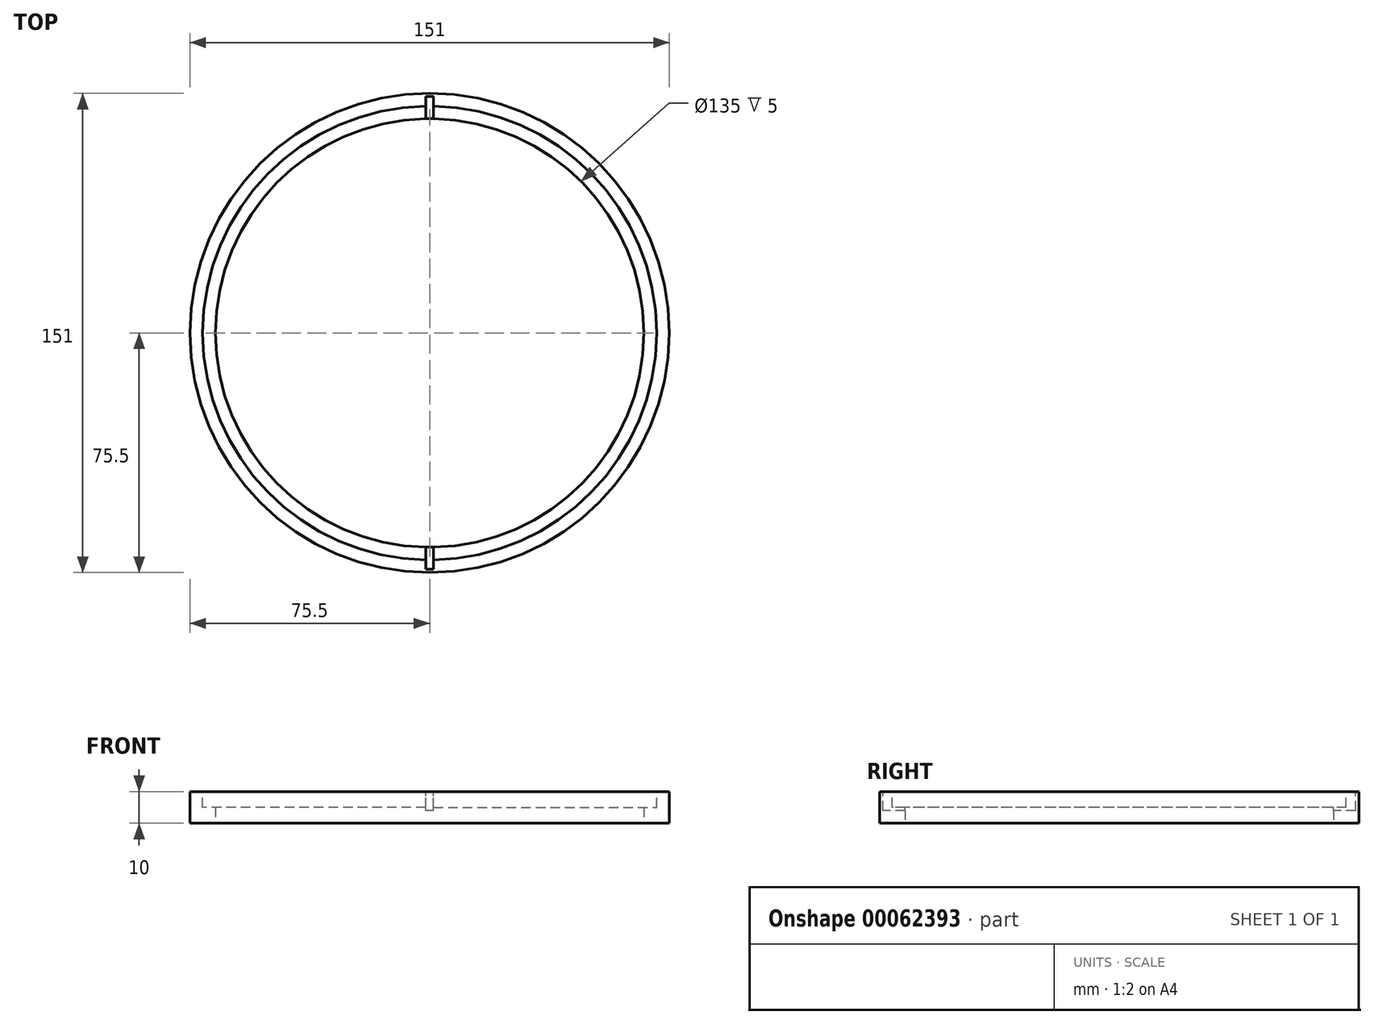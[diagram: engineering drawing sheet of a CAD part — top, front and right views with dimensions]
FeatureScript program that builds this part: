
annotation { "Feature Type Name" : "Feature", "Feature Type Description" : "" }
export const myFeature = defineFeature(function(context is Context, id is Id, definition is map)
    precondition{}
    {
        {
            var Q0;
            Q0=qCreatedBy(makeId("Top.planeOp"),FACE);
            var sketch = newSketch(context, id + "F0", { "sketchPlane" : qUnion([Q0])});
            skCircle(sketch, "E0", {"center": v(0, 0) * mm, "radius": 75.5 * mm});
            skCircle(sketch, "E1", {"center": v(0, 0) * mm, "radius": 67.5 * mm});
            skSolve(sketch);
        }
        {
            var Q0;
            Q0=makeQuery(id+"F0.imprint","IMPRINT",FACE,{"disambiguationData":[TD([[makeQuery(id+"F0.imprint","IMPRINT",EDGE,{"derivedFrom":sQuery(id+"F0.wireOp",EDGE,"E0")}),1.0]])]});
            extrude(context, id + "F1", {"entities" : qUnion([Q0]), "depth" : 10 * mm});
        }
        {
            var Q0;
            Q0=makeQuery(id+"F1.opExtrude","CAP_FACE",FACE,{"disambiguationData":[OSD([sQuery(id+"F0.wireOp",EDGE,"E0"),sQuery(id+"F0.wireOp",EDGE,"E1")])],"isStart":false});
            var sketch = newSketch(context, id + "F2", { "sketchPlane" : qUnion([Q0])});
            skPoint(sketch, "E2", {"position": v(0, 0) * mm});
            skLineSegment(sketch, "E3.rect.bottom", {"start": v(1.25, 74.5) * mm, "end": v(-1.25, 74.5) * mm});
            skLineSegment(sketch, "E3.rect.top", {"start": v(1.25, -74.5) * mm, "end": v(-1.25, -74.5) * mm});
            skLineSegment(sketch, "E3.rect.left", {"start": v(1.25, 74.5) * mm, "end": v(1.25, -74.5) * mm});
            skLineSegment(sketch, "E3.rect.right", {"start": v(-1.25, 74.5) * mm, "end": v(-1.25, -74.5) * mm});
            skCircle(sketch, "E4", {"center": v(0, 0) * mm, "radius": 71.5 * mm});
            skSolve(sketch);
        }
        {
            var Q0;
            {var subQ0=sQuery(id+"F2.wireOp",EDGE,"E3.rect.bottom");Q0=makeQuery(id+"F2.imprint","IMPRINT",FACE,{"disambiguationData":[TD([[makeQuery(id+"F2.imprint","IMPRINT",EDGE,{"derivedFrom":subQ0}),1.0]])]});}
            var Q1;
            {var subQ0=sQuery(id+"F2.wireOp",EDGE,"E4");var subQ1=sQuery(id+"F2.wireOp",EDGE,"E3.rect.left");var subQ2=makeQuery(id+"F2.imprint","INTERSECT",VERTEX,{"disambiguationData":[OD(0.0)],"derivedFrom":[subQ1,subQ0]});Q1=makeQuery(id+"F2.imprint","IMPRINT",FACE,{"disambiguationData":[TD([[makeQuery(id+"F2.imprint","IMPRINT",EDGE,{"disambiguationData":[TD([[subQ2,-1.0]])],"derivedFrom":subQ1}),-1.0]])]});}
            var Q2;
            {var subQ0=sQuery(id+"F2.wireOp",EDGE,"E4");var subQ1=sQuery(id+"F2.wireOp",EDGE,"E3.rect.left");var subQ2=makeQuery(id+"F2.imprint","INTERSECT",VERTEX,{"disambiguationData":[OD(1.0)],"derivedFrom":[subQ1,subQ0]});Q2=makeQuery(id+"F2.imprint","IMPRINT",FACE,{"disambiguationData":[TD([[makeQuery(id+"F2.imprint","IMPRINT",EDGE,{"disambiguationData":[TD([[subQ2,1.0]])],"derivedFrom":subQ1}),-1.0]])]});}
            var Q3;
            {var subQ0=sQuery(id+"F2.wireOp",EDGE,"E3.rect.top");Q3=makeQuery(id+"F2.imprint","IMPRINT",FACE,{"disambiguationData":[TD([[makeQuery(id+"F2.imprint","IMPRINT",EDGE,{"derivedFrom":subQ0}),-1.0]])]});}
            extrude(context, id + "F3", {"entities" : qUnion([Q0, Q1, Q2, Q3]), "operationType" : NewBodyOperationType.REMOVE, "oppositeDirection" : true, "depth" : 6 * mm});
        }
        {
            var Q0;
            {var subQ0=sQuery(id+"F2.wireOp",EDGE,"E4");var subQ1=sQuery(id+"F2.wireOp",EDGE,"E3.rect.left");var subQ2=makeQuery(id+"F2.imprint","INTERSECT",VERTEX,{"disambiguationData":[OD(0.0)],"derivedFrom":[subQ1,subQ0]});Q0=makeQuery(id+"F2.imprint","IMPRINT",FACE,{"disambiguationData":[TD([[makeQuery(id+"F2.imprint","IMPRINT",EDGE,{"disambiguationData":[TD([[subQ2,-1.0]])],"derivedFrom":subQ1}),1.0]])]});}
            var Q1;
            {var subQ0=sQuery(id+"F2.wireOp",EDGE,"E4");var subQ1=sQuery(id+"F2.wireOp",EDGE,"E3.rect.right");var subQ2=makeQuery(id+"F2.imprint","INTERSECT",VERTEX,{"disambiguationData":[OD(0.0)],"derivedFrom":[subQ1,subQ0]});Q1=makeQuery(id+"F2.imprint","IMPRINT",FACE,{"disambiguationData":[TD([[makeQuery(id+"F2.imprint","IMPRINT",EDGE,{"disambiguationData":[TD([[subQ2,-1.0]])],"derivedFrom":subQ1}),-1.0]])]});}
            extrude(context, id + "F4", {"entities" : qUnion([Q0, Q1]), "operationType" : NewBodyOperationType.REMOVE, "oppositeDirection" : true, "depth" : 5 * mm});
        }
    });
